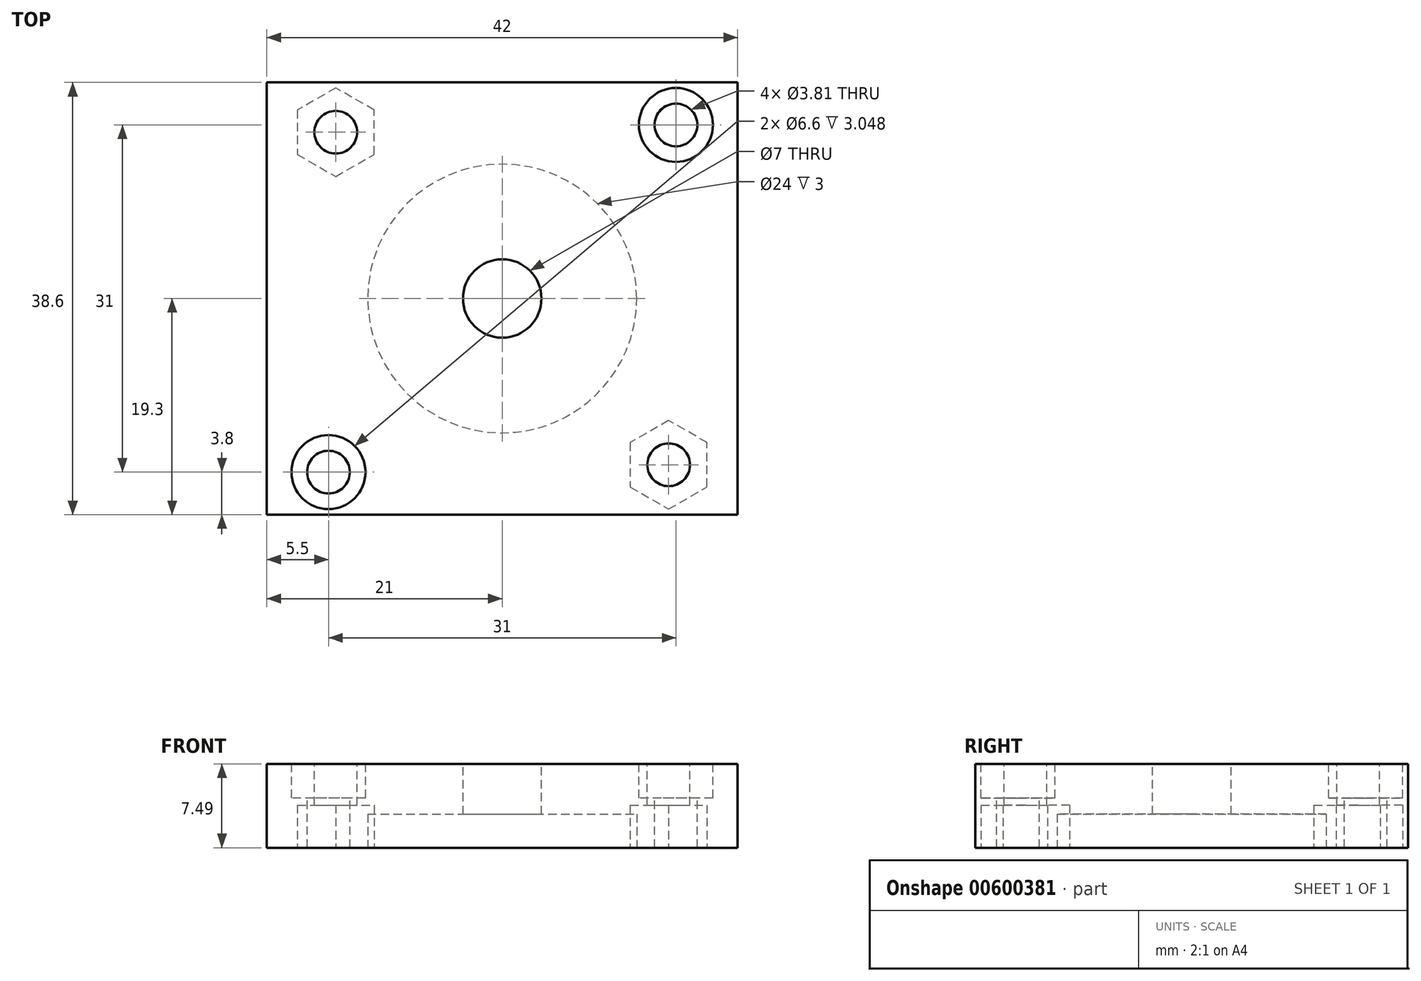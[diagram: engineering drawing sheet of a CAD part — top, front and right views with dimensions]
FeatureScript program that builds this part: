
annotation { "Feature Type Name" : "Feature", "Feature Type Description" : "" }
export const myFeature = defineFeature(function(context is Context, id is Id, definition is map)
    precondition{}
    {
        {
            var Q0;
            Q0=qCreatedBy(makeId("Top.planeOp"),FACE);
            var sketch = newSketch(context, id + "F0", { "sketchPlane" : qUnion([Q0])});
            skLineSegment(sketch, "E0.bottom", {"start": v(21, 19.3) * mm, "end": v(-21, 19.3) * mm});
            skLineSegment(sketch, "E0.top", {"start": v(21, -19.3) * mm, "end": v(-21, -19.3) * mm});
            skLineSegment(sketch, "E0.left", {"start": v(21, 19.3) * mm, "end": v(21, -19.3) * mm});
            skLineSegment(sketch, "E0.right", {"start": v(-21, 19.3) * mm, "end": v(-21, -19.3) * mm});
            skPoint(sketch, "E0.middle", {"position": v(0, 0) * mm});
            skSolve(sketch);
        }
        {
            var Q0;
            Q0 = qSketchRegion(id + "F0", true);
            extrude(context, id + "F1", {"entities" : qUnion([Q0]), "depth" : 7.5 * mm, "offsetDistance" : 25.4 * mm});
        }
        {
            var Q0;
            Q0=makeQuery(id+"F1.opExtrude","CAP_FACE",FACE,{"disambiguationData":[OSD([sQuery(id+"F0.wireOp",EDGE,"E0.bottom"),sQuery(id+"F0.wireOp",EDGE,"E0.top"),sQuery(id+"F0.wireOp",EDGE,"E0.left"),sQuery(id+"F0.wireOp",EDGE,"E0.right")])],"isStart":false});
            var sketch = newSketch(context, id + "F2", { "sketchPlane" : qUnion([Q0])});
            skCircle(sketch, "E1", {"center": v(-14.85, 14.85) * mm, "radius": 1.9 * mm});
            skCircle(sketch, "E2", {"center": v(14.85, -14.85) * mm, "radius": 1.9 * mm});
            skLineSegment(sketch, "E3", {"start": v(-14.85, 14.85) * mm, "end": v(14.85, -14.85) * mm, "construction": true});
            skLineSegment(sketch, "E4.bottom", {"start": v(-14.85, 14.85) * mm, "end": v(14.85, 14.85) * mm, "construction": true});
            skLineSegment(sketch, "E4.top", {"start": v(-14.85, -14.85) * mm, "end": v(14.85, -14.85) * mm, "construction": true});
            skLineSegment(sketch, "E4.left", {"start": v(-14.85, 14.85) * mm, "end": v(-14.85, -14.85) * mm, "construction": true});
            skLineSegment(sketch, "E4.right", {"start": v(14.85, 14.85) * mm, "end": v(14.85, -14.85) * mm, "construction": true});
            skPoint(sketch, "E4.middle", {"position": v(0, 0) * mm});
            skSolve(sketch);
        }
        {
            var Q0;
            Q0 = qSketchRegion(id + "F2", true);
            extrude(context, id + "F3", {"entities" : qUnion([Q0]), "operationType" : NewBodyOperationType.REMOVE, "endBound" : BoundingType.THROUGH_ALL, "oppositeDirection" : true, "depth" : 25.4 * mm, "offsetDistance" : 25.4 * mm});
        }
        {
            var Q0;
            Q0=makeQuery(id+"F1.opExtrude","CAP_FACE",FACE,{"disambiguationData":[OSD([sQuery(id+"F0.wireOp",EDGE,"E0.bottom"),sQuery(id+"F0.wireOp",EDGE,"E0.top"),sQuery(id+"F0.wireOp",EDGE,"E0.left"),sQuery(id+"F0.wireOp",EDGE,"E0.right")])],"isStart":false});
            var sketch = newSketch(context, id + "F4", { "sketchPlane" : qUnion([Q0])});
            skCircle(sketch, "E5", {"center": v(0, 0) * mm, "radius": 21.92 * mm, "construction": true});
            skPoint(sketch, "E6", {"position": v(15.5, 15.5) * mm});
            skPoint(sketch, "E7", {"position": v(15.5, -15.5) * mm});
            skPoint(sketch, "E8", {"position": v(-15.5, -15.5) * mm});
            skPoint(sketch, "E9", {"position": v(-15.5, 15.5) * mm});
            skCircle(sketch, "E10", {"center": v(15.5, 15.5) * mm, "radius": 1.9 * mm});
            skCircle(sketch, "E11", {"center": v(15.5, -15.5) * mm, "radius": 1.9 * mm});
            skCircle(sketch, "E12", {"center": v(-15.5, -15.5) * mm, "radius": 1.9 * mm});
            skCircle(sketch, "E13", {"center": v(-15.5, 15.5) * mm, "radius": 1.9 * mm});
            skLineSegment(sketch, "E14.bottom", {"start": v(-15.5, 15.5) * mm, "end": v(15.5, 15.5) * mm, "construction": true});
            skLineSegment(sketch, "E14.top", {"start": v(-15.5, -15.5) * mm, "end": v(15.5, -15.5) * mm, "construction": true});
            skLineSegment(sketch, "E14.left", {"start": v(-15.5, 15.5) * mm, "end": v(-15.5, -15.5) * mm, "construction": true});
            skLineSegment(sketch, "E14.right", {"start": v(15.5, 15.5) * mm, "end": v(15.5, -15.5) * mm, "construction": true});
            skSolve(sketch);
        }
        {
            var Q0;
            Q0=makeQuery(id+"F4.imprint","IMPRINT",FACE,{"disambiguationData":[TD([[makeQuery(id+"F4.imprint","IMPRINT",EDGE,{"derivedFrom":sQuery(id+"F4.wireOp",EDGE,"E10")}),1.0]])]});
            var Q1;
            Q1=makeQuery(id+"F4.imprint","IMPRINT",FACE,{"disambiguationData":[TD([[makeQuery(id+"F4.imprint","IMPRINT",EDGE,{"derivedFrom":sQuery(id+"F4.wireOp",EDGE,"E12")}),1.0]])]});
            extrude(context, id + "F5", {"entities" : qUnion([Q0, Q1]), "operationType" : NewBodyOperationType.REMOVE, "oppositeDirection" : true, "depth" : 25.4 * mm, "offsetDistance" : 25.4 * mm});
        }
        {
            var Q0;
            Q0=makeQuery(id+"F1.opExtrude","CAP_FACE",FACE,{"disambiguationData":[OSD([sQuery(id+"F0.wireOp",EDGE,"E0.bottom"),sQuery(id+"F0.wireOp",EDGE,"E0.top"),sQuery(id+"F0.wireOp",EDGE,"E0.left"),sQuery(id+"F0.wireOp",EDGE,"E0.right")])],"isStart":false});
            var sketch = newSketch(context, id + "F6", { "sketchPlane" : qUnion([Q0])});
            skCircle(sketch, "E15", {"center": v(15.5, 15.5) * mm, "radius": 3.3 * mm});
            skCircle(sketch, "E16", {"center": v(15.5, 0) * mm, "radius": 3.3 * mm});
            skCircle(sketch, "E17", {"center": v(-15.5, -15.5) * mm, "radius": 3.3 * mm});
            skCircle(sketch, "E18", {"center": v(-15.5, 0) * mm, "radius": 3.3 * mm});
            skSolve(sketch);
        }
        {
            var Q0;
            Q0=makeQuery(id+"F6.imprint","IMPRINT",FACE,{"disambiguationData":[TD([[makeQuery(id+"F6.imprint","IMPRINT",EDGE,{"derivedFrom":makeQuery(id+"F5.boolean.opBoolean","COPY",EDGE,{"derivedFrom":makeQuery(id+"F5.opExtrude","CAP_EDGE",EDGE,{"disambiguationData":[OSD([sQuery(id+"F4.wireOp",EDGE,"E10")])],"isStart":true})})}),1.0]])]});
            var Q1;
            Q1=makeQuery(id+"F6.imprint","IMPRINT",FACE,{"disambiguationData":[TD([[makeQuery(id+"F6.imprint","IMPRINT",EDGE,{"derivedFrom":makeQuery(id+"F5.boolean.opBoolean","COPY",EDGE,{"derivedFrom":makeQuery(id+"F5.opExtrude","CAP_EDGE",EDGE,{"disambiguationData":[OSD([sQuery(id+"F4.wireOp",EDGE,"E11")])],"isStart":true})})}),1.0]])]});
            var Q2;
            Q2=makeQuery(id+"F6.imprint","IMPRINT",FACE,{"disambiguationData":[TD([[makeQuery(id+"F6.imprint","IMPRINT",EDGE,{"derivedFrom":makeQuery(id+"F5.boolean.opBoolean","COPY",EDGE,{"derivedFrom":makeQuery(id+"F5.opExtrude","CAP_EDGE",EDGE,{"disambiguationData":[OSD([sQuery(id+"F4.wireOp",EDGE,"E12")])],"isStart":true})})}),1.0]])]});
            var Q3;
            Q3=makeQuery(id+"F6.imprint","IMPRINT",FACE,{"disambiguationData":[TD([[makeQuery(id+"F6.imprint","IMPRINT",EDGE,{"derivedFrom":makeQuery(id+"F5.boolean.opBoolean","COPY",EDGE,{"derivedFrom":makeQuery(id+"F5.opExtrude","CAP_EDGE",EDGE,{"disambiguationData":[OSD([sQuery(id+"F4.wireOp",EDGE,"E13")])],"isStart":true})})}),1.0]])]});
            var Q4;
            Q4=makeQuery(id+"F6.imprint","IMPRINT",FACE,{"disambiguationData":[TD([[makeQuery(id+"F6.imprint","IMPRINT",EDGE,{"derivedFrom":sQuery(id+"F6.wireOp",EDGE,"E15")}),1.0]])]});
            var Q5;
            Q5=makeQuery(id+"F6.imprint","IMPRINT",FACE,{"disambiguationData":[TD([[makeQuery(id+"F6.imprint","IMPRINT",EDGE,{"derivedFrom":sQuery(id+"F6.wireOp",EDGE,"E17")}),1.0]])]});
            extrude(context, id + "F7", {"entities" : qUnion([Q0, Q1, Q2, Q3, Q4, Q5]), "operationType" : NewBodyOperationType.REMOVE, "oppositeDirection" : true, "depth" : 3.05 * mm, "offsetDistance" : 25.4 * mm});
        }
        {
            var Q0;
            Q0=makeQuery(id+"F1.opExtrude","CAP_FACE",FACE,{"disambiguationData":[OSD([sQuery(id+"F0.wireOp",EDGE,"E0.bottom"),sQuery(id+"F0.wireOp",EDGE,"E0.top"),sQuery(id+"F0.wireOp",EDGE,"E0.left"),sQuery(id+"F0.wireOp",EDGE,"E0.right")])],"isStart":false});
            var sketch = newSketch(context, id + "F8", { "sketchPlane" : qUnion([Q0])});
            skCircle(sketch, "E19", {"center": v(0, 0) * mm, "radius": 3.5 * mm});
            skSolve(sketch);
        }
        {
            var Q0;
            Q0 = qSketchRegion(id + "F8", true);
            extrude(context, id + "F9", {"entities" : qUnion([Q0]), "operationType" : NewBodyOperationType.REMOVE, "endBound" : BoundingType.THROUGH_ALL, "oppositeDirection" : true, "depth" : 25.4 * mm, "offsetDistance" : 25.4 * mm});
        }
        {
            var Q0;
            Q0=makeQuery(id+"F1.opExtrude","CAP_FACE",FACE,{"disambiguationData":[OSD([sQuery(id+"F0.wireOp",EDGE,"E0.bottom"),sQuery(id+"F0.wireOp",EDGE,"E0.top"),sQuery(id+"F0.wireOp",EDGE,"E0.left"),sQuery(id+"F0.wireOp",EDGE,"E0.right")])],"isStart":true});
            var sketch = newSketch(context, id + "F10", { "sketchPlane" : qUnion([Q0])});
            skCircle(sketch, "E20", {"center": v(0, 0) * mm, "radius": 12 * mm});
            skSolve(sketch);
        }
        {
            var Q0;
            Q0 = qSketchRegion(id + "F10", true);
            extrude(context, id + "F11", {"entities" : qUnion([Q0]), "operationType" : NewBodyOperationType.REMOVE, "oppositeDirection" : true, "depth" : 3 * mm, "offsetDistance" : 25.4 * mm});
        }
        {
            var Q0;
            Q0=makeQuery(id+"F1.opExtrude","CAP_FACE",FACE,{"disambiguationData":[OSD([sQuery(id+"F0.wireOp",EDGE,"E0.bottom"),sQuery(id+"F0.wireOp",EDGE,"E0.top"),sQuery(id+"F0.wireOp",EDGE,"E0.left"),sQuery(id+"F0.wireOp",EDGE,"E0.right")])],"isStart":true});
            var sketch = newSketch(context, id + "F12", { "sketchPlane" : qUnion([Q0])});
            skCircle(sketch, "E21.cCircle", {"center": v(14.85, 14.85) * mm, "radius": 3.96 * mm, "construction": true});
            skLineSegment(sketch, "E21.0", {"start": v(18.28, 16.83) * mm, "end": v(18.28, 12.87) * mm});
            skLineSegment(sketch, "E21.1", {"start": v(18.28, 12.87) * mm, "end": v(14.85, 10.89) * mm});
            skLineSegment(sketch, "E21.2", {"start": v(14.85, 10.89) * mm, "end": v(11.42, 12.87) * mm});
            skLineSegment(sketch, "E21.3", {"start": v(11.42, 12.87) * mm, "end": v(11.42, 16.83) * mm});
            skLineSegment(sketch, "E21.4", {"start": v(11.42, 16.83) * mm, "end": v(14.85, 18.8) * mm});
            skLineSegment(sketch, "E21.5", {"start": v(14.85, 18.8) * mm, "end": v(18.28, 16.83) * mm});
            skCircle(sketch, "E22.cCircle", {"center": v(-14.85, -14.85) * mm, "radius": 3.96 * mm, "construction": true});
            skLineSegment(sketch, "E22.0", {"start": v(-11.42, -12.87) * mm, "end": v(-11.42, -16.83) * mm});
            skLineSegment(sketch, "E22.1", {"start": v(-11.42, -16.83) * mm, "end": v(-14.85, -18.8) * mm});
            skLineSegment(sketch, "E22.2", {"start": v(-14.85, -18.8) * mm, "end": v(-18.28, -16.83) * mm});
            skLineSegment(sketch, "E22.3", {"start": v(-18.28, -16.83) * mm, "end": v(-18.28, -12.87) * mm});
            skLineSegment(sketch, "E22.4", {"start": v(-18.28, -12.87) * mm, "end": v(-14.85, -10.89) * mm});
            skLineSegment(sketch, "E22.5", {"start": v(-14.85, -10.89) * mm, "end": v(-11.42, -12.87) * mm});
            skSolve(sketch);
        }
        {
            var Q0;
            Q0 = qSketchRegion(id + "F12", true);
            extrude(context, id + "F13", {"entities" : qUnion([Q0]), "operationType" : NewBodyOperationType.REMOVE, "oppositeDirection" : true, "depth" : 3.8 * mm, "offsetDistance" : 25.4 * mm});
        }
    });
